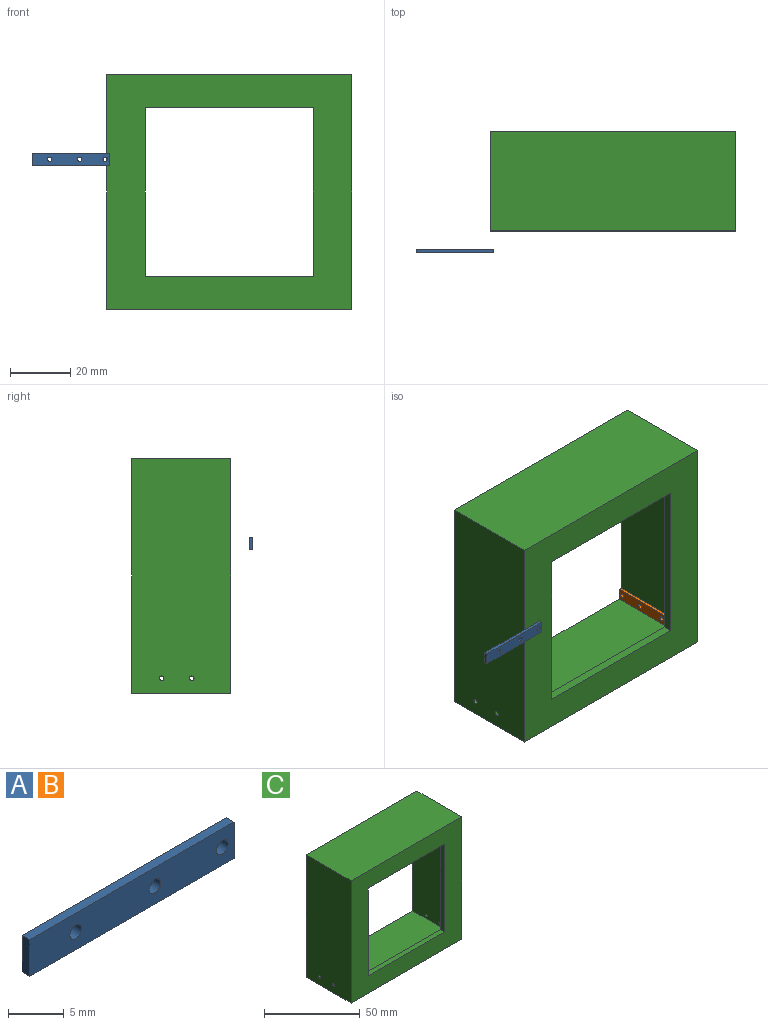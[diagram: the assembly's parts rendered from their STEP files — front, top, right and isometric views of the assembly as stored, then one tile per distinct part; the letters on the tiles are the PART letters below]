
ASSEMBLY  parts=3 mates=1
PART A: 9 faces, bbox 25.8x1x4 mm
  f0: plane 25.81x1mm, normal (0,0,1), area 25.8mm2, adj f1,f6,f7,f8
  f1: plane 4x1mm, normal (-1,0,0), area 4mm2, adj f0,f2,f7,f8
  f2: plane 25.81x1mm, normal (0,0,-1), area 25.8mm2, adj f1,f6,f7,f8
  f3: cylinder r=0.75mm len=1.5mm, axis (0,1,0), area 4.7mm2, adj f7,f8
  f4: cylinder r=0.75mm len=1.5mm, axis (0,1,0), area 4.7mm2, adj f7,f8
  f5: cylinder r=0.75mm len=1.5mm, axis (0,1,0), area 4.7mm2, adj f7,f8
  f6: plane 4x1mm, normal (1,0,0), area 4mm2, adj f0,f2,f7,f8
  f7: plane 25.81x4mm, normal (0,-1,0), area 97.9mm2, adj f0,f1,f2,f3,f4,f5,f6
  f8: plane 25.81x4mm, normal (0,1,0), area 97.9mm2, adj f0,f1,f2,f3,f4,f5,f6
PART B: same geometry as A
PART C: 19 faces, bbox 81.5x33x78 mm
  f0: plane 75.5x30mm, normal (0,0,-1), area 2265mm2, adj f1,f3,f9,f14
  f1: plane 72x30mm, normal (-1,0,0), area 2156.5mm2, adj f0,f2,f9,f14,f17,f18
  f2: plane 75.5x30mm, normal (0,0,1), area 2265mm2, adj f1,f3,f9,f14
  f3: plane 72x30mm, normal (1,0,0), area 2156.5mm2, adj f0,f2,f9,f14,f15,f16
  f4: plane 78x33mm, normal (1,0,0), area 2570.5mm2, adj f5,f7,f8,f9,f17,f18
  f5: plane 81.5x33mm, normal (0,0,1), area 2689.5mm2, adj f4,f6,f8,f9
  f6: plane 78x33mm, normal (-1,0,0), area 2570.5mm2, adj f5,f7,f8,f9,f15,f16
  f7: plane 81.5x33mm, normal (0,0,-1), area 2689.5mm2, adj f4,f6,f8,f9
  f8: plane 81.5x78mm, normal (0,-1,0), area 3221mm2, adj f4,f5,f6,f7,f10,f11,f12,f13
  f9: plane 81.5x78mm, normal (0,1,0), area 921mm2, adj f0,f1,f2,f3,f4,f5,f6,f7
  f10: plane 56x3mm, normal (0,0,-1), area 168mm2, adj f8,f11,f13,f14
  f11: plane 56x3mm, normal (-1,0,0), area 168mm2, adj f8,f10,f12,f14
  f12: plane 56x3mm, normal (0,0,1), area 168mm2, adj f8,f11,f13,f14
  f13: plane 56x3mm, normal (1,0,0), area 168mm2, adj f8,f10,f12,f14
  f14: plane 75.5x72mm, normal (0,1,0), area 2300mm2, adj f0,f1,f2,f3,f10,f11,f12,f13
  f15: cylinder r=0.75mm len=3mm, axis (1,0,0), area 14.1mm2, adj f3,f6
  f16: cylinder r=0.75mm len=3mm, axis (1,0,0), area 14.1mm2, adj f3,f6
  f17: cylinder r=0.75mm len=3mm, axis (1,0,0), area 14.1mm2, adj f1,f4
  f18: cylinder r=0.75mm len=3mm, axis (1,0,0), area 14.1mm2, adj f1,f4
PLACE A t=(-60.32,-22.99,17.67)mm
PLACE B rot(axis=(0,0,1),90deg) t=(28.33,4.02,-27.22)mm
PLACE C t=(-8.42,16.16,6.78)mm
MATE fastened B.f3 <-> C.f15  axis (1,0,0) through (29.33,-3.84,-27.22)mm
